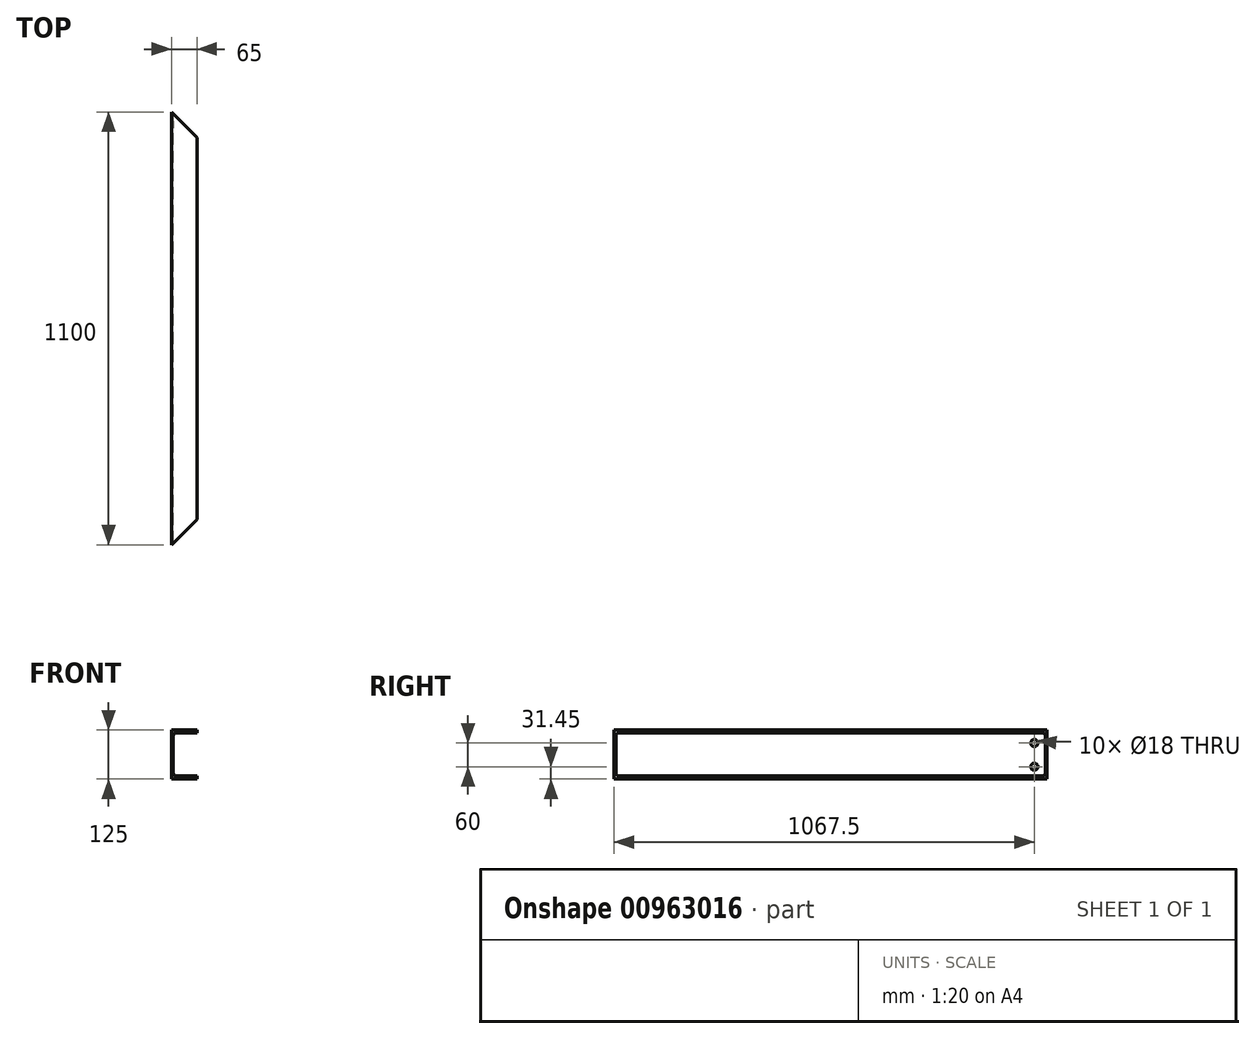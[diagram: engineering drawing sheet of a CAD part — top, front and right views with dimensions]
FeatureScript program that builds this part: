
annotation { "Feature Type Name" : "Feature", "Feature Type Description" : "" }
export const myFeature = defineFeature(function(context is Context, id is Id, definition is map)
    precondition{}
    {
        {
            var Q0;
            Q0=qCreatedBy(makeId("Front.planeOp"),FACE);
            var sketch = newSketch(context, id + "F0", { "sketchPlane" : qUnion([Q0])});
            skLineSegment(sketch, "E0", {"start": v(-25.08, -61.45) * mm, "end": v(-25.08, 63.55) * mm});
            skLineSegment(sketch, "E1", {"start": v(-25.08, 63.55) * mm, "end": v(39.92, 63.55) * mm});
            skLineSegment(sketch, "E2", {"start": v(39.92, 63.55) * mm, "end": v(39.92, 56.05) * mm});
            skLineSegment(sketch, "E3", {"start": v(39.92, 56.05) * mm, "end": v(-12.38, 56.05) * mm});
            skLineSegment(sketch, "E4", {"start": v(-25.08, -61.45) * mm, "end": v(39.92, -61.45) * mm});
            skLineSegment(sketch, "E5", {"start": v(39.92, -61.45) * mm, "end": v(39.92, -53.95) * mm});
            skLineSegment(sketch, "E6", {"start": v(39.92, -53.95) * mm, "end": v(-12.38, -53.95) * mm});
            skLineSegment(sketch, "E7", {"start": v(-20.38, -45.95) * mm, "end": v(-20.38, 48.05) * mm});
            skPoint(sketch, "E8.visualSharp", {"position": v(-20.38, 56.05) * mm});
            skArc(sketch, "E8.filletArc", {"start": v(-12.38, 56.05) * mm, "mid": v(-18.03, 53.7) * mm, "end": v(-20.38, 48.05) * mm});
            skPoint(sketch, "E9.visualSharp", {"position": v(-20.38, -53.95) * mm});
            skArc(sketch, "E9.filletArc", {"start": v(-20.38, -45.95) * mm, "mid": v(-18.03, -51.61) * mm, "end": v(-12.38, -53.95) * mm});
            skSolve(sketch);
        }
        {
            var Q0;
            Q0=makeQuery(id+"F0.imprint","IMPRINT",FACE,{"disambiguationData":[TD([[makeQuery(id+"F0.imprint","IMPRINT",EDGE,{"derivedFrom":sQuery(id+"F0.wireOp",EDGE,"E0")}),-1.0]])]});
            extrude(context, id + "F1", {"entities" : qUnion([Q0]), "depth" : 1100 * mm, "offsetDistance" : 25 * mm});
        }
        {
            var Q0;
            Q0=makeQuery(id+"F1.opExtrude","SWEPT_FACE",FACE,{"disambiguationData":[OSD([sQuery(id+"F0.wireOp",EDGE,"E1")])]});
            var sketch = newSketch(context, id + "F2", { "sketchPlane" : qUnion([Q0])});
            skLineSegment(sketch, "E10", {"start": v(39.92, -1100) * mm, "end": v(39.92, -1035) * mm});
            skLineSegment(sketch, "E11", {"start": v(39.92, -1035) * mm, "end": v(-25.08, -1100) * mm});
            skLineSegment(sketch, "E12", {"start": v(39.92, 0) * mm, "end": v(39.92, -65) * mm});
            skLineSegment(sketch, "E13", {"start": v(39.92, -65) * mm, "end": v(-25.08, 0) * mm});
            skSolve(sketch);
        }
        {
            var Q0;
            Q0=makeQuery(id+"F2.imprint","IMPRINT",FACE,{"disambiguationData":[TD([[makeQuery(id+"F2.imprint","IMPRINT",EDGE,{"derivedFrom":sQuery(id+"F2.wireOp",EDGE,"E12")}),1.0]])]});
            var Q1;
            Q1=makeQuery(id+"F2.imprint","IMPRINT",FACE,{"disambiguationData":[TD([[makeQuery(id+"F2.imprint","IMPRINT",EDGE,{"derivedFrom":sQuery(id+"F2.wireOp",EDGE,"E10")}),1.0]])]});
            extrude(context, id + "F3", {"entities" : qUnion([Q0, Q1]), "operationType" : NewBodyOperationType.REMOVE, "endBound" : BoundingType.THROUGH_ALL, "oppositeDirection" : true, "depth" : 25 * mm, "offsetDistance" : 25 * mm});
        }
        {
            var Q0;
            Q0=makeQuery(id+"F1.opExtrude","SWEPT_FACE",FACE,{"disambiguationData":[OSD([sQuery(id+"F0.wireOp",EDGE,"E0")])]});
            var sketch = newSketch(context, id + "F4", { "sketchPlane" : qUnion([Q0])});
            skCircle(sketch, "E14", {"center": v(32.5, 30) * mm, "radius": 9 * mm});
            skCircle(sketch, "E15", {"center": v(32.5, -30) * mm, "radius": 9 * mm});
            skPoint(sketch, "E16.endSnap0", {"position": v(0, 1.05) * mm});
            skSolve(sketch);
        }
        {
            var Q0;
            Q0=qSketchRegion(id+"F4",true);
            extrude(context, id + "F5", {"entities" : qUnion([Q0]), "operationType" : NewBodyOperationType.REMOVE, "endBound" : BoundingType.THROUGH_ALL, "oppositeDirection" : true, "depth" : 25 * mm, "offsetDistance" : 25 * mm});
        }
    });
